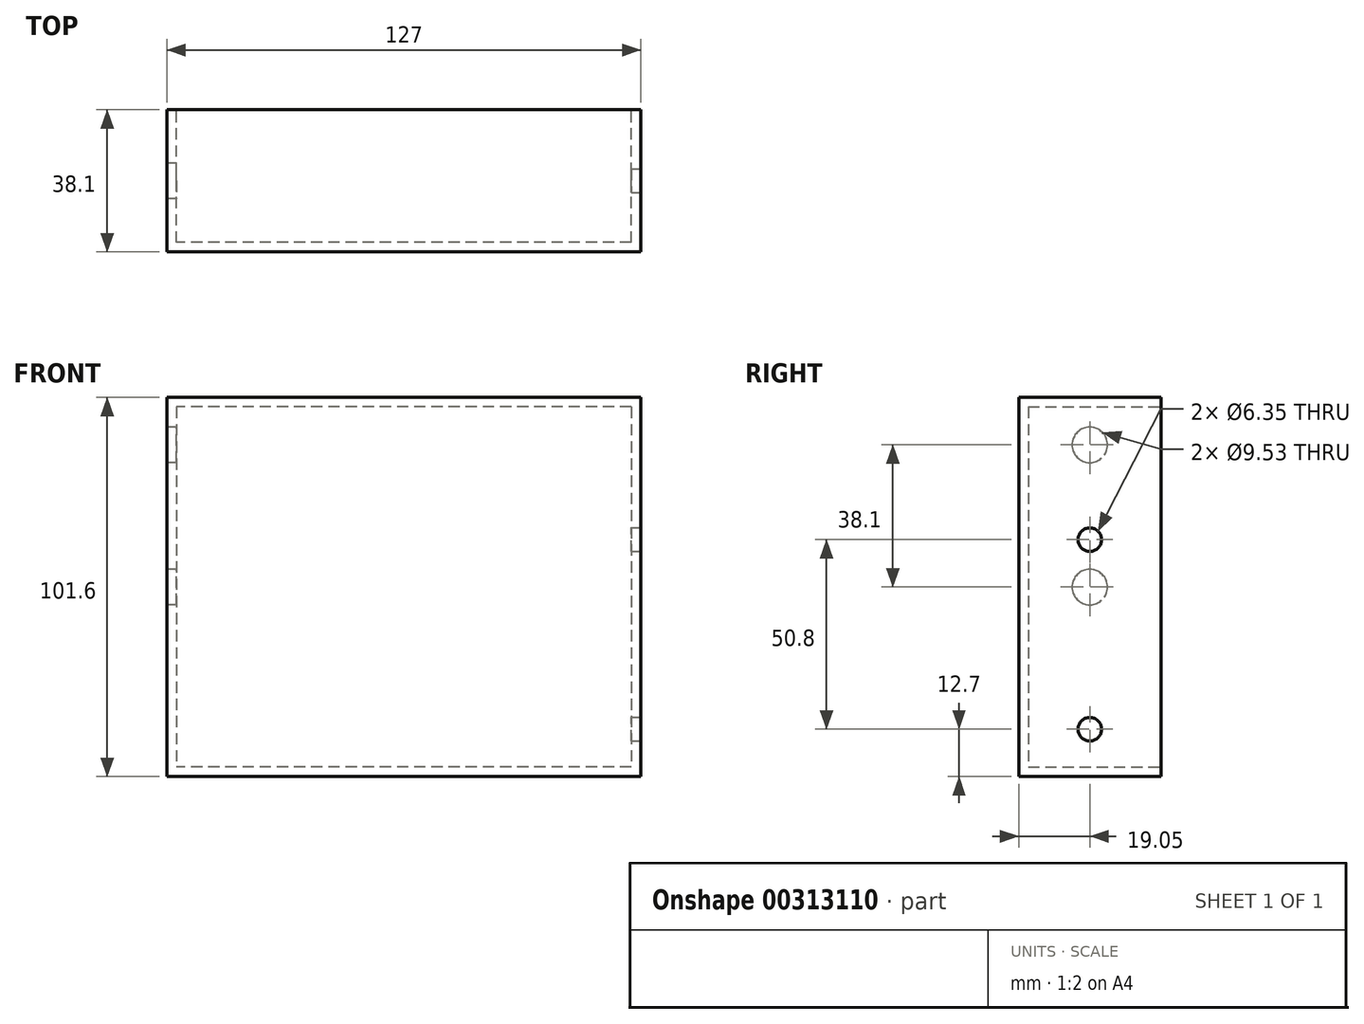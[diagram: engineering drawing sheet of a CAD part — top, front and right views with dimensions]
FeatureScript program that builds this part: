
annotation { "Feature Type Name" : "Feature", "Feature Type Description" : "" }
export const myFeature = defineFeature(function(context is Context, id is Id, definition is map)
    precondition{}
    {
        {
            var Q0;
            Q0=qCreatedBy(makeId("Front.planeOp"),FACE);
            var sketch = newSketch(context, id + "F0", { "sketchPlane" : qUnion([Q0])});
            skLineSegment(sketch, "E0.bottom", {"start": v(63.5, 50.8) * mm, "end": v(-63.5, 50.8) * mm});
            skLineSegment(sketch, "E0.top", {"start": v(63.5, -50.8) * mm, "end": v(-63.5, -50.8) * mm});
            skLineSegment(sketch, "E0.left", {"start": v(63.5, 50.8) * mm, "end": v(63.5, -50.8) * mm});
            skLineSegment(sketch, "E0.right", {"start": v(-63.5, 50.8) * mm, "end": v(-63.5, -50.8) * mm});
            skPoint(sketch, "E0.middle", {"position": v(0, 0) * mm});
            skSolve(sketch);
        }
        {
            var Q0;
            Q0 = qSketchRegion(id + "F0", true);
            extrude(context, id + "F1", {"entities" : qUnion([Q0]), "endBound" : BoundingType.SYMMETRIC, "depth" : 38.1 * mm});
        }
        {
            var Q0;
            Q0=makeQuery(id+"F1.opExtrude","CAP_FACE",FACE,{"disambiguationData":[OSD([sQuery(id+"F0.wireOp",EDGE,"E0.bottom"),sQuery(id+"F0.wireOp",EDGE,"E0.top"),sQuery(id+"F0.wireOp",EDGE,"E0.left"),sQuery(id+"F0.wireOp",EDGE,"E0.right")])],"isStart":true});
            shell(context, id + "F2", {"entities" : qUnion([Q0]), "thickness" : 2.54 * mm});
        }
        {
            var Q0;
            Q0=makeQuery(id+"F1.opExtrude","SWEPT_FACE",FACE,{"disambiguationData":[OSD([sQuery(id+"F0.wireOp",EDGE,"E0.left")])]});
            var sketch = newSketch(context, id + "F3", { "sketchPlane" : qUnion([Q0])});
            skCircle(sketch, "E1", {"center": v(0, -38.1) * mm, "radius": 3.18 * mm});
            skPoint(sketch, "E1.centerSnap0", {"position": v(0, -50.8) * mm});
            skCircle(sketch, "E2", {"center": v(0, 12.7) * mm, "radius": 3.18 * mm});
            skSolve(sketch);
        }
        {
            var Q0;
            Q0 = qSketchRegion(id + "F3", true);
            extrude(context, id + "F4", {"entities" : qUnion([Q0]), "operationType" : NewBodyOperationType.REMOVE, "endBound" : BoundingType.UP_TO_NEXT, "oppositeDirection" : true, "depth" : 25.4 * mm});
        }
        {
            var Q0;
            Q0=makeQuery(id+"F1.opExtrude","SWEPT_FACE",FACE,{"disambiguationData":[OSD([sQuery(id+"F0.wireOp",EDGE,"E0.right")])]});
            var sketch = newSketch(context, id + "F5", { "sketchPlane" : qUnion([Q0])});
            skCircle(sketch, "E3", {"center": v(0, 38.1) * mm, "radius": 4.76 * mm});
            skPoint(sketch, "E3.centerSnap0", {"position": v(0, -50.8) * mm});
            skCircle(sketch, "E4", {"center": v(0, 0) * mm, "radius": 4.76 * mm});
            skSolve(sketch);
        }
        {
            var Q0;
            Q0 = qSketchRegion(id + "F5", true);
            extrude(context, id + "F6", {"entities" : qUnion([Q0]), "operationType" : NewBodyOperationType.REMOVE, "endBound" : BoundingType.UP_TO_NEXT, "oppositeDirection" : true, "depth" : 25.4 * mm});
        }
    });
